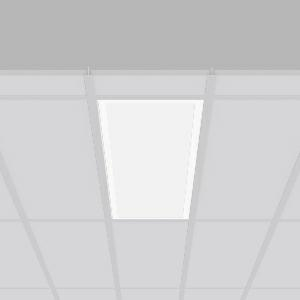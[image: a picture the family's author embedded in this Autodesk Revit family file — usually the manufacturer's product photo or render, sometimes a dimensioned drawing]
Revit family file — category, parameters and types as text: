
# Revit family: sidelite_eco_672376_002_1_2179
name_source: partatom
category: Lighting Fixtures
units: mm (PartAtom-declared; Revit-internal decimal feet)

## family parameters
Cut with Voids When Loaded = No
Host = Face
Light Source = No
Part Type = Normal
Room Calculation Point = No
Round Connector Dimension = Use Diameter
Shared = No

## types (1)
- SIDELITE ECO (1 x LED Modul 840, 3500 lm, 4000)
    Apparent Load = 29 VA
    CIE Flux Codes = 47 79 96 100 100
    Color Rendering = 80
    Color Temperature = 4000
    Default Elevation = 1800 mm
    Description = Series: SIDELITE ECO
Highly economical recessed luminaire with progressive LED technology. For escape route illumination. Frame made of aluminium, powder-coated. Diffuser: plastic, opal. Lightguide and diffuser made of non-yellowing plastic (PMMA). Lateral light emission (RZB SIDELITE technology) for homogeneous light distribution. External driver. Second cable inlet for loop through. External driver with simple plug-in locking system. Extended connection cable (1.90 m). Suitable for connection to central battery systems. 
Colour: white
Length: 1245 mm
Width: 308 mm
Cut-out length: 1220 mm
Cut-out width: 285 mm
Recess height: 160 mm
Luminaire: recess height: 40 mm
Weight: 3.64 kg
Operating mode: maintained power mode
Lamp: LED
Socket: without socket
Colour temperature: 4000K
Colour rendering index (CRI): 80
System power: 29 W
Rated luminous flux: 3500 lm
Luminous flux, emergency: 3500 lm
System power, emergency: 29 W
Control gear: Regulated power supply
Protection class: II
Type of protection: IP 20
    Height = 0 mm  [stored 0 ft]
    Lamp = 1 x LED Modul 840
    Lamp Light Flux = 3500 lm
    Lamp count = 1
    Length = 1245 mm
    Lifetime = 50000 h
    Luminous efficacy = 121 lm/W
    Manufacturer = RZB
    ModVariant = No
    Model = 672376.002.1
    Mounting Place = Ceiling
    Mounting Type = Recessed
    Number of Poles = 1
    OnlyDefault = Yes
    Power Factor = 1
    Product Name = SIDELITE ECO
    Product group = Recessed modular luminaires
    ProductGroupID = 406
    Protection Class = Protection class II
    Protection Degree = IP 20
    RLX_Detail_Level = 1
    RLX_Emergency_Light_Flux = 3500 lm
    RLX_Emergency_Type = 3
    RLX_Emergency_Type_DB = Yes
    RlxData = <blob elided: 30037 chars, md5=b53ed4b9>
    Socket = socket
    Standby Power = 0 W
    System Light Flux = 3500 lm
    System Power = 29 W
    Type Comments = Product without accessories
    Type Image = 312367.002.jpg
    URL = http://relux.com
    VarID = ---
    Voltage = 230 V
    Voltage Range = 220-240 V
    Weight = 0.00 kg
    Width = 308 mm

note: [stored X ft] marks values corroborated as IEEE doubles in the binary element streams (Revit-internal decimal feet)

## geometry (parser evidence)
native form markers: Blend x4, Sweep x10
no freeform markers — native parametric forms only
